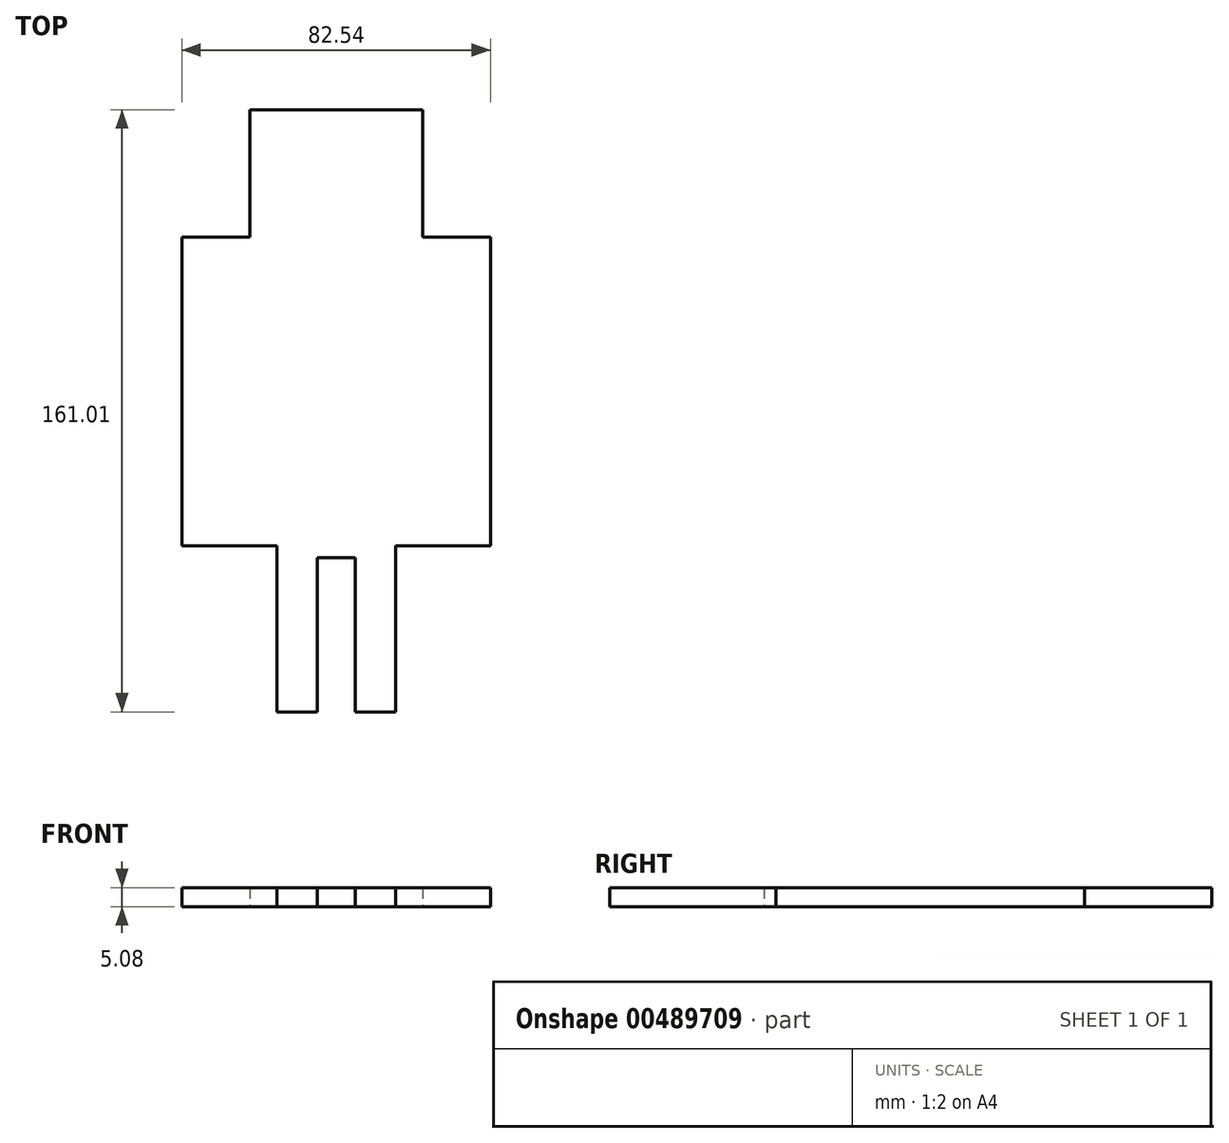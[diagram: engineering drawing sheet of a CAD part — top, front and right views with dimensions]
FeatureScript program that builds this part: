
annotation { "Feature Type Name" : "Feature", "Feature Type Description" : "" }
export const myFeature = defineFeature(function(context is Context, id is Id, definition is map)
    precondition{}
    {
        {
            var Q0;
            Q0=qCreatedBy(makeId("Top.planeOp"),FACE);
            var sketch = newSketch(context, id + "F0", { "sketchPlane" : qUnion([Q0])});
            skLineSegment(sketch, "E0.bottom", {"start": v(41.27, 41.28) * mm, "end": v(23.1, 41.28) * mm});
            skLineSegment(sketch, "E0.top", {"start": v(41.28, -41.28) * mm, "end": v(15.88, -41.28) * mm});
            skLineSegment(sketch, "E0.left", {"start": v(41.27, 41.28) * mm, "end": v(41.28, -41.28) * mm});
            skLineSegment(sketch, "E0.right", {"start": v(-41.28, 41.28) * mm, "end": v(-41.27, -41.28) * mm});
            skPoint(sketch, "E0.middle", {"position": v(0, 0) * mm});
            skLineSegment(sketch, "E1.bottom", {"start": v(23.1, 75.3) * mm, "end": v(-23.1, 75.3) * mm});
            skLineSegment(sketch, "E1.left", {"start": v(23.1, 75.3) * mm, "end": v(23.1, 41.28) * mm});
            skLineSegment(sketch, "E1.right", {"start": v(-23.1, 75.3) * mm, "end": v(-23.1, 41.28) * mm});
            skPoint(sketch, "E1.middle", {"position": v(0, 41.28) * mm});
            skPoint(sketch, "E2.orphan", {"position": v(23.1, 7.26) * mm});
            skPoint(sketch, "E3.orphan", {"position": v(-23.1, 7.26) * mm});
            skLineSegment(sketch, "E4.top", {"start": v(15.88, -85.73) * mm, "end": v(5.08, -85.73) * mm});
            skLineSegment(sketch, "E4.left", {"start": v(15.88, -41.28) * mm, "end": v(15.88, -85.73) * mm});
            skLineSegment(sketch, "E4.right", {"start": v(-15.87, -41.28) * mm, "end": v(-15.87, -85.73) * mm});
            skPoint(sketch, "E4.middle", {"position": v(0, -41.28) * mm});
            skPoint(sketch, "E5.orphan", {"position": v(-15.87, 3.18) * mm});
            skPoint(sketch, "E6.orphan", {"position": v(15.88, 3.17) * mm});
            skPoint(sketch, "E7.middle", {"position": v(0, -85.73) * mm});
            skPoint(sketch, "E7.top.end.orphan", {"position": v(-4.98, -127) * mm});
            skPoint(sketch, "E7.top.start.orphan", {"position": v(4.73, -127) * mm});
            skLineSegment(sketch, "E8.bottom", {"start": v(5.08, -44.45) * mm, "end": v(-5.08, -44.45) * mm});
            skLineSegment(sketch, "E8.top", {"start": v(5.08, -127) * mm, "end": v(4.73, -127) * mm});
            skLineSegment(sketch, "E8.left", {"start": v(5.08, -44.45) * mm, "end": v(5.08, -85.73) * mm});
            skLineSegment(sketch, "E8.right", {"start": v(-5.08, -44.45) * mm, "end": v(-5.08, -85.73) * mm});
            skLineSegment(sketch, "E9.trimOffspring", {"start": v(-5.08, -85.73) * mm, "end": v(-15.87, -85.73) * mm});
            skPoint(sketch, "E10.trimOffspring.end.orphan", {"position": v(-5.08, -127) * mm});
            skLineSegment(sketch, "E11.trimOffspring", {"start": v(-15.87, -41.28) * mm, "end": v(-41.27, -41.28) * mm});
            skLineSegment(sketch, "E12.trimOffspring", {"start": v(-23.1, 41.28) * mm, "end": v(-41.28, 41.28) * mm});
            skSolve(sketch);
        }
        {
            var Q0;
            Q0=makeQuery(id+"F0.imprint","IMPRINT",FACE,{"disambiguationData":[TD([[makeQuery(id+"F0.imprint","IMPRINT",EDGE,{"derivedFrom":sQuery(id+"F0.wireOp",EDGE,"E0.bottom")}),1.0]])]});
            extrude(context, id + "F1", {"entities" : qUnion([Q0]), "depth" : 5.08 * mm});
        }
    });
